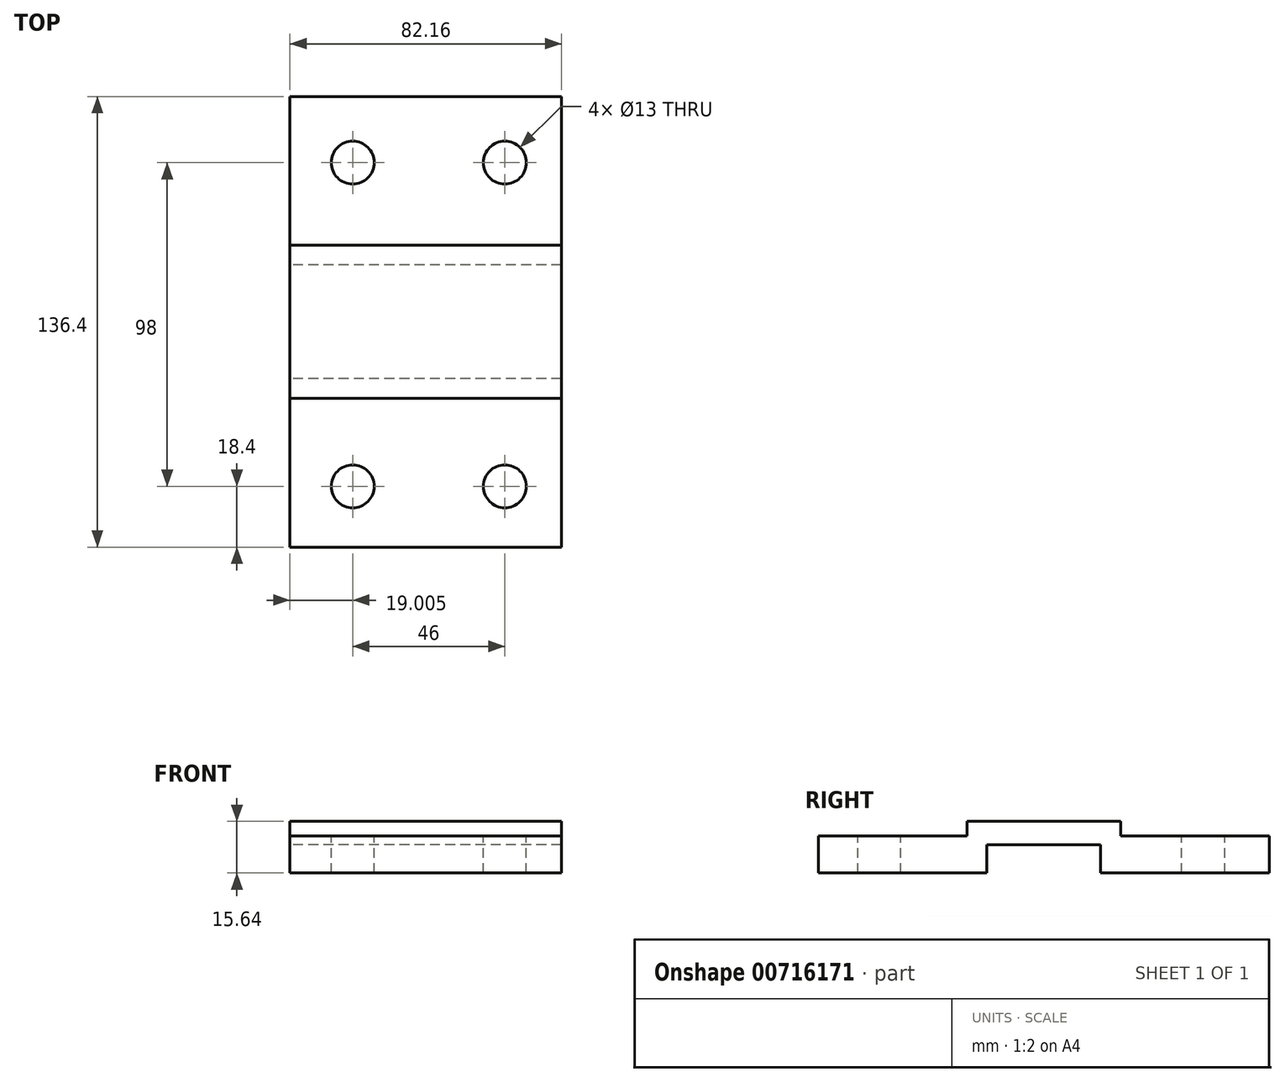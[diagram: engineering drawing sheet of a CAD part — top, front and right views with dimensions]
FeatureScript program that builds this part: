
annotation { "Feature Type Name" : "Feature", "Feature Type Description" : "" }
export const myFeature = defineFeature(function(context is Context, id is Id, definition is map)
    precondition{}
    {
        {
            var Q0;
            Q0=qCreatedBy(makeId("Right.planeOp"),FACE);
            var sketch = newSketch(context, id + "F0", { "sketchPlane" : qUnion([Q0])});
            skLineSegment(sketch, "E0", {"start": v(-51, -8.5) * mm, "end": v(0, -8.5) * mm});
            skLineSegment(sketch, "E1", {"start": v(0, -8.5) * mm, "end": v(0, 0) * mm});
            skLineSegment(sketch, "E2", {"start": v(0, 0) * mm, "end": v(34.4, 0) * mm});
            skLineSegment(sketch, "E3", {"start": v(34.4, 0) * mm, "end": v(34.4, -8.5) * mm});
            skLineSegment(sketch, "E4", {"start": v(34.4, -8.5) * mm, "end": v(85.4, -8.5) * mm});
            skLineSegment(sketch, "E5", {"start": v(40.4, 2.74) * mm, "end": v(40.4, 7.14) * mm});
            skLineSegment(sketch, "E6", {"start": v(40.4, 7.14) * mm, "end": v(-6, 7.14) * mm});
            skLineSegment(sketch, "E7", {"start": v(-6, 7.14) * mm, "end": v(-6, 2.74) * mm});
            skLineSegment(sketch, "E8", {"start": v(-51, -8.5) * mm, "end": v(-51, 2.74) * mm});
            skLineSegment(sketch, "E9", {"start": v(85.4, -8.5) * mm, "end": v(85.4, 2.74) * mm});
            skLineSegment(sketch, "E10", {"start": v(-51, 2.74) * mm, "end": v(-6, 2.74) * mm});
            skLineSegment(sketch, "E11", {"start": v(40.4, 2.74) * mm, "end": v(85.4, 2.74) * mm});
            skSolve(sketch);
        }
        {
            var Q0;
            Q0=makeQuery(id+"F0.imprint","IMPRINT",FACE,{"disambiguationData":[TD([[makeQuery(id+"F0.imprint","IMPRINT",EDGE,{"derivedFrom":sQuery(id+"F0.wireOp",EDGE,"E0")}),1.0]])]});
            extrude(context, id + "F1", {"entities" : qUnion([Q0]), "endBound" : BoundingType.SYMMETRIC, "depth" : 82.15 * mm, "offsetDistance" : 25 * mm});
        }
        {
            var Q0;
            Q0=makeQuery(id+"F1.opExtrude","SWEPT_FACE",FACE,{"disambiguationData":[OSD([sQuery(id+"F0.wireOp",EDGE,"E11")])]});
            var sketch = newSketch(context, id + "F2", { "sketchPlane" : qUnion([Q0])});
            skPoint(sketch, "E12", {"position": v(-22.07, 65.4) * mm});
            skPoint(sketch, "E13.0.1.0", {"position": v(-22.07, -32.6) * mm});
            skPoint(sketch, "E13.1.0.0", {"position": v(23.92, 65.4) * mm});
            skPoint(sketch, "E13.1.1.0", {"position": v(23.92, -32.6) * mm});
            skLineSegment(sketch, "E13.direction1", {"start": v(-22.07, 65.4) * mm, "end": v(23.92, 65.4) * mm, "construction": true});
            skLineSegment(sketch, "E13.direction2", {"start": v(-22.07, 65.4) * mm, "end": v(-22.07, -32.6) * mm, "construction": true});
            skSolve(sketch);
        }
        {
            var Q0;
            Q0=sQuery(id+"F2.wireOp",VERTEX,"E12");
            var Q1;
            Q1=sQuery(id+"F2.wireOp",VERTEX,"E13.1.0.0");
            var Q2;
            Q2=sQuery(id+"F2.wireOp",VERTEX,"E13.1.1.0");
            var Q3;
            Q3=sQuery(id+"F2.wireOp",VERTEX,"E13.0.1.0");
            var Q4;
            Q4=makeQuery(id+"F1.opExtrude","SWEPT_BODY",BODY,{"disambiguationData":[OSD([sQuery(id+"F0.wireOp",EDGE,"E0"),sQuery(id+"F0.wireOp",EDGE,"E1"),sQuery(id+"F0.wireOp",EDGE,"E2"),sQuery(id+"F0.wireOp",EDGE,"E3"),sQuery(id+"F0.wireOp",EDGE,"E4"),sQuery(id+"F0.wireOp",EDGE,"E5"),sQuery(id+"F0.wireOp",EDGE,"E6"),sQuery(id+"F0.wireOp",EDGE,"E7"),sQuery(id+"F0.wireOp",EDGE,"E8"),sQuery(id+"F0.wireOp",EDGE,"E9"),sQuery(id+"F0.wireOp",EDGE,"E10"),sQuery(id+"F0.wireOp",EDGE,"E11")])]});
            hole(context, id + "F3", {"style" : HoleStyle.SIMPLE, "endStyle" : HoleEndStyle.THROUGH, "holeDiameter" : 13 * mm, "majorDiameter" : 5 * mm, "isTappedThrough" : true, "tappedDepth" : 12 * mm, "tapClearance" : 0, "locations" : qUnion([Q0, Q1, Q2, Q3]), "scope" : qUnion([Q4])});
        }
    });
